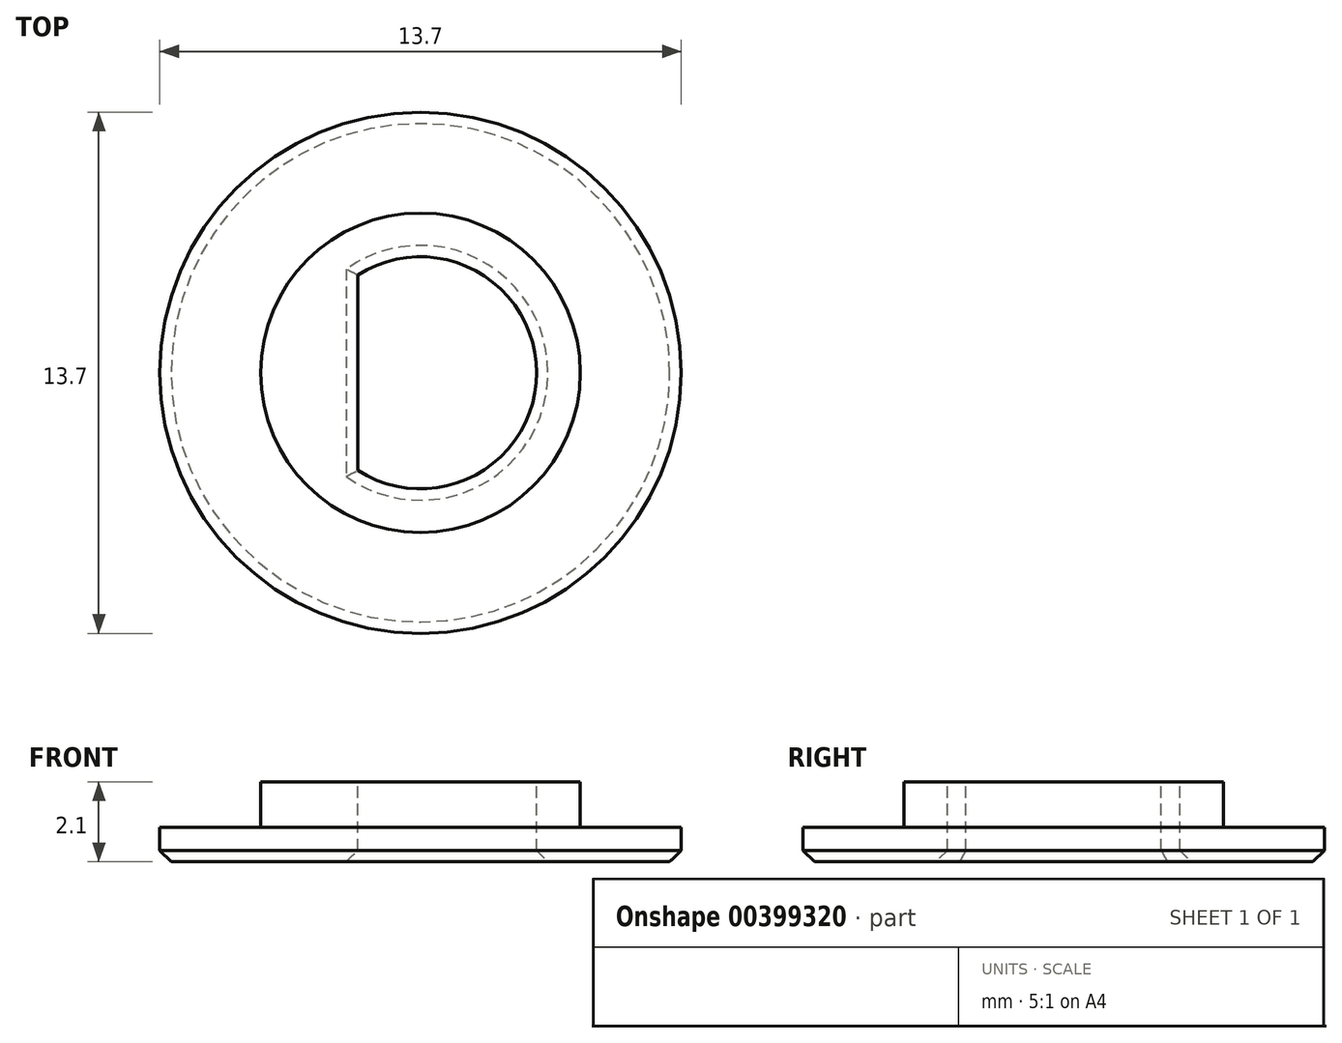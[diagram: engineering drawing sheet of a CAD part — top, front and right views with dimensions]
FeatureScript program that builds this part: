
annotation { "Feature Type Name" : "Feature", "Feature Type Description" : "" }
export const myFeature = defineFeature(function(context is Context, id is Id, definition is map)
    precondition{}
    {
        {
            var Q0;
            Q0=qCreatedBy(makeId("Top.planeOp"),FACE);
            var sketch = newSketch(context, id + "F0", { "sketchPlane" : qUnion([Q0])});
            skCircle(sketch, "E0", {"center": v(0, 0) * mm, "radius": 6.85 * mm});
            skSolve(sketch);
        }
        {
            var Q0;
            Q0=makeQuery(id+"F0.imprint","IMPRINT",FACE,{"disambiguationData":[TD([[makeQuery(id+"F0.imprint","IMPRINT",EDGE,{"derivedFrom":sQuery(id+"F0.wireOp",EDGE,"E0")}),1.0]])]});
            extrude(context, id + "F1", {"entities" : qUnion([Q0]), "depth" : 0.9 * mm});
        }
        {
            var Q0;
            Q0=makeQuery(id+"F1.opExtrude","CAP_FACE",FACE,{"disambiguationData":[OSD([sQuery(id+"F0.wireOp",EDGE,"E0")])],"isStart":false});
            var sketch = newSketch(context, id + "F2", { "sketchPlane" : qUnion([Q0])});
            skCircle(sketch, "E1", {"center": v(0, 0) * mm, "radius": 4.2 * mm});
            skSolve(sketch);
        }
        {
            var Q0;
            Q0=makeQuery(id+"F2.imprint","IMPRINT",FACE,{"disambiguationData":[TD([[makeQuery(id+"F2.imprint","IMPRINT",EDGE,{"derivedFrom":sQuery(id+"F2.wireOp",EDGE,"E1")}),1.0]])]});
            extrude(context, id + "F3", {"entities" : qUnion([Q0]), "operationType" : NewBodyOperationType.ADD, "depth" : 1.2 * mm});
        }
        {
            var Q0;
            Q0=makeQuery(id+"F3.opExtrude","CAP_FACE",FACE,{"disambiguationData":[OSD([sQuery(id+"F2.wireOp",EDGE,"E1")])],"isStart":false});
            var sketch = newSketch(context, id + "F4", { "sketchPlane" : qUnion([Q0])});
            skCircle(sketch, "E2", {"center": v(0, 0) * mm, "radius": 3.05 * mm});
            skLineSegment(sketch, "E3", {"start": v(-1.65, 2.57) * mm, "end": v(-1.65, -2.57) * mm});
            skSolve(sketch);
        }
        {
            var Q0;
            {var subQ0=sQuery(id+"F4.wireOp",EDGE,"E3");Q0=makeQuery(id+"F4.imprint","IMPRINT",FACE,{"disambiguationData":[TD([[makeQuery(id+"F4.imprint","IMPRINT",EDGE,{"derivedFrom":subQ0}),1.0]])]});}
            var Q1;
            Q1=makeQuery(id+"F1.opExtrude","CAP_FACE",FACE,{"disambiguationData":[OSD([sQuery(id+"F0.wireOp",EDGE,"E0")])],"isStart":true});
            extrude(context, id + "F5", {"entities" : qUnion([Q0]), "operationType" : NewBodyOperationType.REMOVE, "endBound" : BoundingType.UP_TO_SURFACE, "oppositeDirection" : true, "endBoundEntityFace" : qUnion([Q1]), "depth" : 25 * mm});
        }
        {
            var Q0;
            Q0=makeQuery(id+"F1.opExtrude","CAP_FACE",FACE,{"disambiguationData":[OSD([sQuery(id+"F0.wireOp",EDGE,"E0")])],"isStart":true});
            chamfer(context, id + "F6", {"entities" : qUnion([Q0]), "width" : 0.3 * mm, "tangentPropagation" : true});
        }
    });
